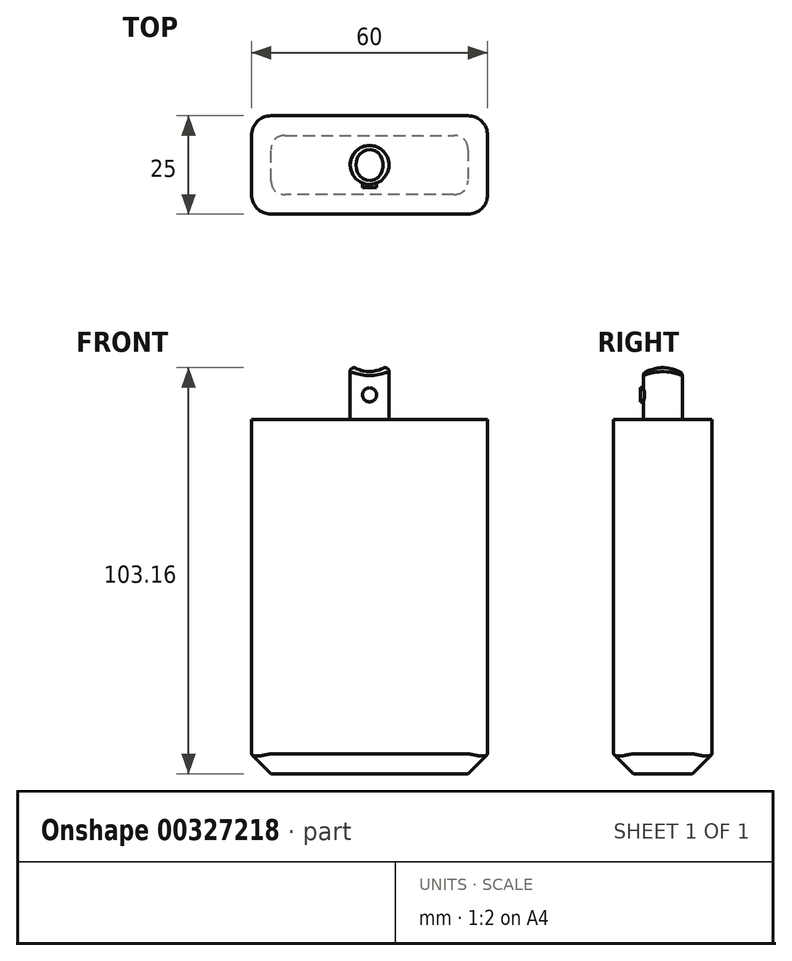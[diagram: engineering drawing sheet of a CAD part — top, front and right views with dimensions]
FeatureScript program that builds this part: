
annotation { "Feature Type Name" : "Feature", "Feature Type Description" : "" }
export const myFeature = defineFeature(function(context is Context, id is Id, definition is map)
    precondition{}
    {
        {
            var Q0;
            Q0=qCreatedBy(makeId("Top.planeOp"),FACE);
            var sketch = newSketch(context, id + "F0", { "sketchPlane" : qUnion([Q0])});
            skLineSegment(sketch, "E0.bottom", {"start": v(-30, -12.5) * mm, "end": v(30, -12.5) * mm});
            skLineSegment(sketch, "E0.top", {"start": v(-30, 12.5) * mm, "end": v(30, 12.5) * mm});
            skLineSegment(sketch, "E0.left", {"start": v(-30, -12.5) * mm, "end": v(-30, 12.5) * mm});
            skLineSegment(sketch, "E0.right", {"start": v(30, -12.5) * mm, "end": v(30, 12.5) * mm});
            skPoint(sketch, "E0.middle", {"position": v(0, 0) * mm});
            skSolve(sketch);
        }
        {
            var Q0;
            Q0 = qSketchRegion(id + "F0", true);
            extrude(context, id + "F1", {"entities" : qUnion([Q0]), "depth" : 90 * mm});
        }
        {
            var Q0;
            Q0=makeQuery(id+"F1.opExtrude","CAP_EDGE",EDGE,{"disambiguationData":[OSD([sQuery(id+"F0.wireOp",EDGE,"E0.left")])],"isStart":true});
            var Q1;
            Q1=makeQuery(id+"F1.opExtrude","CAP_FACE",FACE,{"disambiguationData":[OSD([sQuery(id+"F0.wireOp",EDGE,"E0.bottom"),sQuery(id+"F0.wireOp",EDGE,"E0.top"),sQuery(id+"F0.wireOp",EDGE,"E0.left"),sQuery(id+"F0.wireOp",EDGE,"E0.right")])],"isStart":true});
            chamfer(context, id + "F2", {"entities" : qUnion([Q0, Q1]), "width" : 5 * mm, "tangentPropagation" : true});
        }
        {
            var Q0;
            Q0=makeQuery(id+"F1.opExtrude","SWEPT_EDGE",EDGE,{"disambiguationData":[OSD([sQuery(id+"F0.wireOp",EDGE,"E0.bottom"),sQuery(id+"F0.wireOp",EDGE,"E0.right")])]});
            var Q1;
            Q1=makeQuery(id+"F1.opExtrude","SWEPT_EDGE",EDGE,{"disambiguationData":[OSD([sQuery(id+"F0.wireOp",EDGE,"E0.top"),sQuery(id+"F0.wireOp",EDGE,"E0.right")])]});
            var Q2;
            Q2=makeQuery(id+"F1.opExtrude","SWEPT_EDGE",EDGE,{"disambiguationData":[OSD([sQuery(id+"F0.wireOp",EDGE,"E0.bottom"),sQuery(id+"F0.wireOp",EDGE,"E0.left")])]});
            var Q3;
            Q3=makeQuery(id+"F1.opExtrude","SWEPT_EDGE",EDGE,{"disambiguationData":[OSD([sQuery(id+"F0.wireOp",EDGE,"E0.top"),sQuery(id+"F0.wireOp",EDGE,"E0.left")])]});
            fillet(context, id + "F3", {"entities" : qUnion([Q0, Q1, Q2, Q3]), "radius" : 5 * mm, "tangentPropagation" : true, "allowEdgeOverflow" : false});
        }
        {
            var Q0;
            Q0=makeQuery(id+"F1.opExtrude","CAP_FACE",FACE,{"disambiguationData":[OSD([sQuery(id+"F0.wireOp",EDGE,"E0.bottom"),sQuery(id+"F0.wireOp",EDGE,"E0.top"),sQuery(id+"F0.wireOp",EDGE,"E0.left"),sQuery(id+"F0.wireOp",EDGE,"E0.right")])],"isStart":false});
            var sketch = newSketch(context, id + "F4", { "sketchPlane" : qUnion([Q0])});
            skCircle(sketch, "E1", {"center": v(0, 0) * mm, "radius": 4.95 * mm});
            skSolve(sketch);
        }
        {
            var Q0;
            Q0=makeQuery(id+"F4.imprint","IMPRINT",FACE,{"disambiguationData":[TD([[makeQuery(id+"F4.imprint","IMPRINT",EDGE,{"derivedFrom":sQuery(id+"F4.wireOp",EDGE,"E1")}),1.0]])]});
            extrude(context, id + "F5", {"entities" : qUnion([Q0]), "operationType" : NewBodyOperationType.ADD, "depth" : 15 * mm});
        }
        {
            var Q0;
            Q0=makeQuery(id+"F1.opExtrude","SWEPT_FACE",FACE,{"disambiguationData":[OSD([sQuery(id+"F0.wireOp",EDGE,"E0.bottom")])]});
            var sketch = newSketch(context, id + "F6", { "sketchPlane" : qUnion([Q0])});
            skCircle(sketch, "E2", {"center": v(0, 109.75) * mm, "radius": 7.56 * mm});
            skSolve(sketch);
        }
        {
            var Q0;
            Q0=makeQuery(id+"F6.imprint","IMPRINT",FACE,{"disambiguationData":[TD([[makeQuery(id+"F6.imprint","IMPRINT",EDGE,{"derivedFrom":sQuery(id+"F6.wireOp",EDGE,"E2")}),1.0]])]});
            extrude(context, id + "F7", {"entities" : qUnion([Q0]), "operationType" : NewBodyOperationType.REMOVE, "endBound" : BoundingType.THROUGH_ALL, "oppositeDirection" : true, "depth" : 25 * mm});
        }
        {
            var Q0;
            Q0=makeQuery(id+"F7.boolean.opBoolean","INTERSECT",EDGE,{"derivedFrom":[makeQuery(id+"F5.opExtrude","SWEPT_FACE",FACE,{"disambiguationData":[OSD([sQuery(id+"F4.wireOp",EDGE,"E1")])]}),makeQuery(id+"F7.opExtrude","SWEPT_FACE",FACE,{"disambiguationData":[OSD([sQuery(id+"F6.wireOp",EDGE,"E2")])]})]});
            fillet(context, id + "F8", {"entities" : qUnion([Q0]), "radius" : 1 * mm, "tangentPropagation" : true, "allowEdgeOverflow" : false});
        }
        {
            var Q0;
            Q0=makeQuery(id+"F1.opExtrude","SWEPT_FACE",FACE,{"disambiguationData":[OSD([sQuery(id+"F0.wireOp",EDGE,"E0.bottom")])]});
            var sketch = newSketch(context, id + "F9", { "sketchPlane" : qUnion([Q0])});
            skCircle(sketch, "E3", {"center": v(0, 96.27) * mm, "radius": 1.8 * mm});
            skSolve(sketch);
        }
        {
            var Q0;
            Q0=makeQuery(id+"F9.imprint","IMPRINT",FACE,{"disambiguationData":[TD([[makeQuery(id+"F9.imprint","IMPRINT",EDGE,{"derivedFrom":sQuery(id+"F9.wireOp",EDGE,"E3")}),1.0]])]});
            extrude(context, id + "F10", {"entities" : qUnion([Q0]), "operationType" : NewBodyOperationType.ADD, "oppositeDirection" : true, "depth" : 11 * mm});
        }
        {
            var Q0;
            Q0=makeQuery(id+"F1.opExtrude","SWEPT_FACE",FACE,{"disambiguationData":[OSD([sQuery(id+"F0.wireOp",EDGE,"E0.left")])]});
            var sketch = newSketch(context, id + "F11", { "sketchPlane" : qUnion([Q0])});
            skLineSegment(sketch, "E4.bottom", {"start": v(5.67, 103.28) * mm, "end": v(15.67, 103.28) * mm});
            skLineSegment(sketch, "E4.top", {"start": v(5.67, 92.15) * mm, "end": v(15.67, 92.15) * mm});
            skLineSegment(sketch, "E4.left", {"start": v(5.67, 103.28) * mm, "end": v(5.67, 92.15) * mm});
            skLineSegment(sketch, "E4.right", {"start": v(15.67, 103.28) * mm, "end": v(15.67, 92.15) * mm});
            skSolve(sketch);
        }
        {
            var Q0;
            Q0 = qSketchRegion(id + "F11", true);
            extrude(context, id + "F12", {"entities" : qUnion([Q0]), "operationType" : NewBodyOperationType.REMOVE, "endBound" : BoundingType.THROUGH_ALL, "oppositeDirection" : true, "depth" : 25 * mm});
        }
        {
            var Q0;
            Q0=makeQuery(id+"FE9Y2GPvSLDhF2e_1.opChamfer","BLEND_EDGE",EDGE,{"blendedFrom":[makeQuery(id+"F1.opExtrude","CAP_EDGE",EDGE,{"disambiguationData":[OSD([sQuery(id+"F0.wireOp",EDGE,"E0.bottom")])],"isStart":false}),makeQuery(id+"F1.opExtrude","CAP_EDGE",EDGE,{"disambiguationData":[OSD([sQuery(id+"F0.wireOp",EDGE,"E0.left")])],"isStart":false})],"blendedInto":[]});
            var Q1;
            Q1=makeQuery(id+"FE9Y2GPvSLDhF2e_1.opChamfer","BLEND_EDGE",EDGE,{"blendedFrom":[makeQuery(id+"F1.opExtrude","CAP_EDGE",EDGE,{"disambiguationData":[OSD([sQuery(id+"F0.wireOp",EDGE,"E0.top")])],"isStart":false}),makeQuery(id+"F1.opExtrude","CAP_EDGE",EDGE,{"disambiguationData":[OSD([sQuery(id+"F0.wireOp",EDGE,"E0.left")])],"isStart":false})],"blendedInto":[]});
            var Q2;
            Q2=makeQuery(id+"FE9Y2GPvSLDhF2e_1.opChamfer","BLEND_EDGE",EDGE,{"blendedFrom":[makeQuery(id+"F1.opExtrude","CAP_EDGE",EDGE,{"disambiguationData":[OSD([sQuery(id+"F0.wireOp",EDGE,"E0.bottom")])],"isStart":false}),makeQuery(id+"F1.opExtrude","CAP_EDGE",EDGE,{"disambiguationData":[OSD([sQuery(id+"F0.wireOp",EDGE,"E0.right")])],"isStart":false})],"blendedInto":[]});
            var Q3;
            Q3=makeQuery(id+"F2.opChamfer","BLEND_EDGE",EDGE,{"blendedFrom":[makeQuery(id+"F1.opExtrude","CAP_EDGE",EDGE,{"disambiguationData":[OSD([sQuery(id+"F0.wireOp",EDGE,"E0.bottom")])],"isStart":true}),makeQuery(id+"F1.opExtrude","CAP_EDGE",EDGE,{"disambiguationData":[OSD([sQuery(id+"F0.wireOp",EDGE,"E0.left")])],"isStart":true})],"blendedInto":[]});
            var Q4;
            Q4=makeQuery(id+"F2.opChamfer","BLEND_EDGE",EDGE,{"blendedFrom":[makeQuery(id+"F1.opExtrude","CAP_EDGE",EDGE,{"disambiguationData":[OSD([sQuery(id+"F0.wireOp",EDGE,"E0.top")])],"isStart":true}),makeQuery(id+"F1.opExtrude","CAP_EDGE",EDGE,{"disambiguationData":[OSD([sQuery(id+"F0.wireOp",EDGE,"E0.left")])],"isStart":true})],"blendedInto":[]});
            var Q5;
            Q5=makeQuery(id+"F2.opChamfer","BLEND_EDGE",EDGE,{"blendedFrom":[makeQuery(id+"F1.opExtrude","CAP_EDGE",EDGE,{"disambiguationData":[OSD([sQuery(id+"F0.wireOp",EDGE,"E0.bottom")])],"isStart":true}),makeQuery(id+"F1.opExtrude","CAP_EDGE",EDGE,{"disambiguationData":[OSD([sQuery(id+"F0.wireOp",EDGE,"E0.right")])],"isStart":true})],"blendedInto":[]});
            var Q6;
            Q6=makeQuery(id+"FE9Y2GPvSLDhF2e_1.opChamfer","BLEND_EDGE",EDGE,{"blendedFrom":[makeQuery(id+"F1.opExtrude","CAP_EDGE",EDGE,{"disambiguationData":[OSD([sQuery(id+"F0.wireOp",EDGE,"E0.top")])],"isStart":false}),makeQuery(id+"F1.opExtrude","CAP_EDGE",EDGE,{"disambiguationData":[OSD([sQuery(id+"F0.wireOp",EDGE,"E0.right")])],"isStart":false})],"blendedInto":[]});
            var Q7;
            Q7=makeQuery(id+"F2.opChamfer","BLEND_EDGE",EDGE,{"blendedFrom":[makeQuery(id+"F1.opExtrude","CAP_EDGE",EDGE,{"disambiguationData":[OSD([sQuery(id+"F0.wireOp",EDGE,"E0.top")])],"isStart":true}),makeQuery(id+"F1.opExtrude","CAP_EDGE",EDGE,{"disambiguationData":[OSD([sQuery(id+"F0.wireOp",EDGE,"E0.right")])],"isStart":true})],"blendedInto":[]});
            fillet(context, id + "F13", {"entities" : qUnion([Q0, Q1, Q2, Q3, Q4, Q5, Q6, Q7]), "radius" : 5 * mm, "tangentPropagation" : true, "allowEdgeOverflow" : false});
        }
    });
